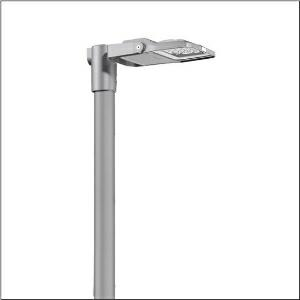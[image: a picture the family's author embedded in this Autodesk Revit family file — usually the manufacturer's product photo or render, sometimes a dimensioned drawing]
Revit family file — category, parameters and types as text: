
# Revit family: floodlight_fl_21_iq_micro___pl61_5xa7761a4c3a_000e
name_source: partatom
category: Lighting Fixtures
units: mm (PartAtom-declared; Revit-internal decimal feet)

## family parameters
Cut with Voids When Loaded = No
Host = Face
Light Source = No
Part Type = Normal
Room Calculation Point = No
Round Connector Dimension = Use Diameter
Shared = No

## types (1)
- --- (1 x LED, 3030 lm, 23.1 W, 4000K)
    Apparent Load = 23 VA
    CIE Flux Codes = 33 65 98 100 100
    Color Rendering = 70
    Color Temperature = 4000K
    Default Elevation = 1800 mm
    Description = Floodlight FL 21 iQ micro, floodlight, primary light control with lens, of PMMA, primary optical cover: protective disc, of toughened safety glass, transparent, light distribution: PL61, light emission: direct distribution, installation type: surface-mounted, LED, High Power LED, rated luminous flux: 3.030lm, luminous efficacy: 131lm/W, light colour: 740, colour temperature: 4000K, control gear: iQ Comfort/DALI, control: optimised constant luminous flux control (CLO 2.0), Desk-Remote (wireless, voltage-free reading and setting of iQ features in the workshop via application-optimized NFC function/RFID function), Light-Fading, Smart-Wire, Night-Set, Lumen-Switch, Temp-Guard, Auto-Match, with terminal, 6-pole, mains connection: 220..240V, AC, 50/60Hz, start of lifetime: 23W, end of service life: 24W, reduction: 11W, luminaire housing, of diecast aluminium, powder-coated, Siteco® metallic grey (DB 702S), corrosivity category C5 mid according to DIN EN ISO 12944, suitable for swimming pools, chlorine-resistant, sealing non-destructively replaceable, please order mast flange separately, mast bracket, of steel, galvanised, powder-coated, Siteco® metallic grey (DB 702S), protection rating (complete): IP66, insulation class (complete): insulation class II (safety insulation), certification: CE, ENEC, VDE, protection symbol: D, impact resistance: IK07, permissible operating ambient temperature: -40..+40°C, permissible operating ambient temperature for outdoor applications: -40..+50°C, standard: DIN EN 12944, LABS conformity tested according to VDMA 24364:2018-05, packaging unit: 1 piece

Light Distribution: PL61
    Height = 65 mm
    Lamp = 1 x LED
    Lamp Light Flux = 3030 lm
    Lamp Power = 23.1 W
    Lamp count = 1
    Length = 312 mm
    Luminous efficacy = 131 lm/W
    Manufacturer = Siteco
    ModVariant = No
    Model = 5XA7761A4C3A
    Number of Poles = 1
    OnlyDefault = Yes
    Power Factor = 1
    Product Name = Floodlight FL 21 iQ micro | PL61
    Product group = floodlight | pylon annexe
    ProductGroupID = 6200
    Protection Class = Protection class II
    Protection Degree = IP 66
    RLX_Detail_Level = 1
    RLX_Emergency_Light_Flux = 0 lm
    RLX_Emergency_Type = 0
    RLX_Emergency_Type_DB = No
    RlxData = <blob elided: 101989 chars, md5=1bfdb502>
    Socket = socket
    Standby Power = 0 W
    System Light Flux = 3030 lm
    System Power = 23 W
    Type Comments = factory setting: luminous flux: 100 % | dim-lin: 254 | 455 mA
    Type Image = l_1007121.jpg
    URL = http://relux.com
    VarID = @adj_194512
    Voltage = 0 V
    Weight = 0.00 kg
    Width = 230 mm

## geometry (parser evidence)
native form markers: Blend x4, Sweep x9
no freeform markers — native parametric forms only
